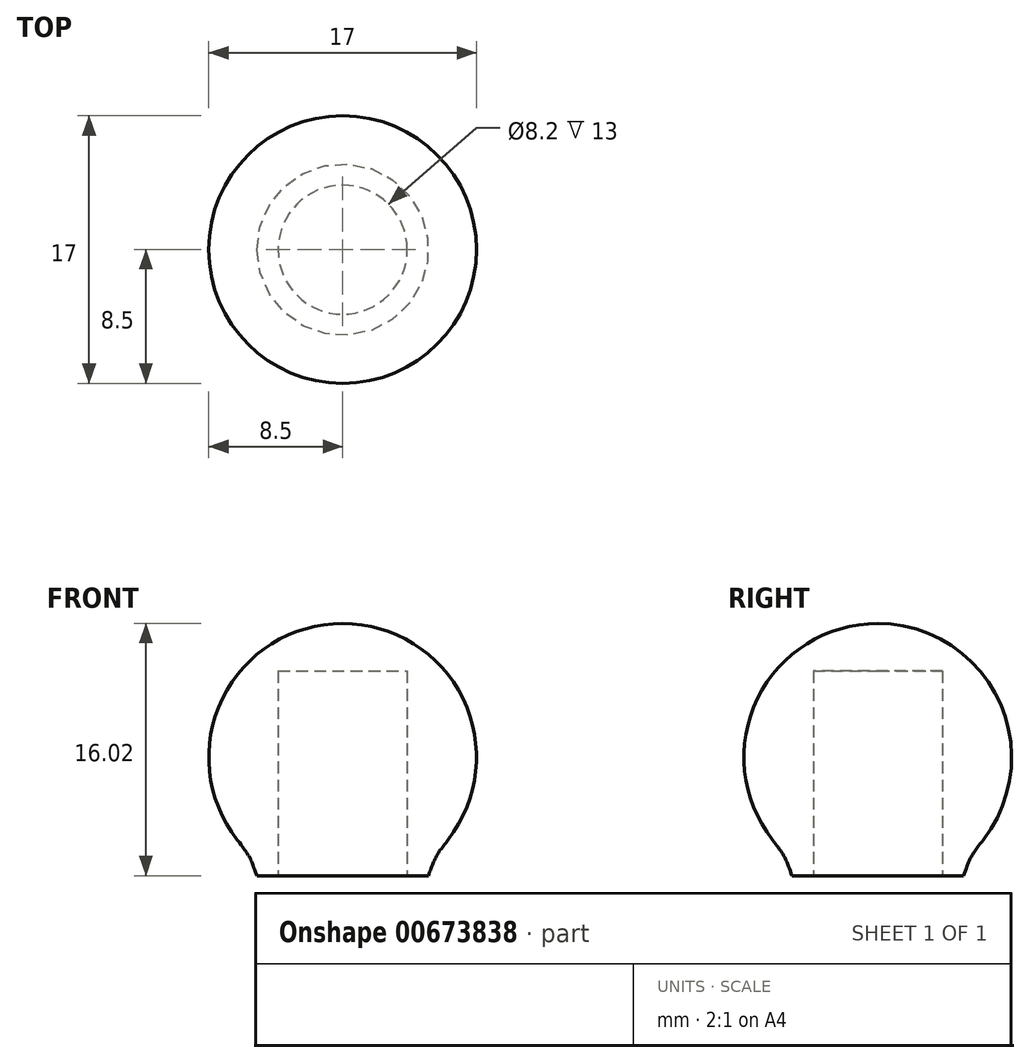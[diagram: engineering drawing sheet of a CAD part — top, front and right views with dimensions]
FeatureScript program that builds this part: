
annotation { "Feature Type Name" : "Feature", "Feature Type Description" : "" }
export const myFeature = defineFeature(function(context is Context, id is Id, definition is map)
    precondition{}
    {
        {
            var Q0;
            Q0=qCreatedBy(makeId("Right.planeOp"),FACE);
            var sketch = newSketch(context, id + "F0", { "sketchPlane" : qUnion([Q0])});
            skLineSegment(sketch, "E0", {"start": v(0, 0) * mm, "end": v(4.1, 0) * mm, "construction": true});
            skArc(sketch, "E1", {"start": v(5.45, 0) * mm, "mid": v(8, 9.42) * mm, "end": v(0, 15.02) * mm});
            skLineSegment(sketch, "E2", {"start": v(0, 0) * mm, "end": v(0, 15.02) * mm, "construction": true});
            skLineSegment(sketch, "E3", {"start": v(4.1, 12) * mm, "end": v(0, 12) * mm});
            skLineSegment(sketch, "E4", {"start": v(0, 12) * mm, "end": v(0, 15.02) * mm});
            skLineSegment(sketch, "E5", {"start": v(4.1, 12) * mm, "end": v(4.1, -1) * mm});
            skLineSegment(sketch, "E6", {"start": v(4.1, -1) * mm, "end": v(5.45, -1) * mm});
            skLineSegment(sketch, "E7", {"start": v(5.45, -1) * mm, "end": v(5.45, 0) * mm});
            skLineSegment(sketch, "E8", {"start": v(5.45, 0) * mm, "end": v(4.1, 0) * mm, "construction": true});
            skSolve(sketch);
        }
        {
            var Q0;
            Q0=makeQuery(id+"F0.imprint","IMPRINT",FACE,{"disambiguationData":[TD([[makeQuery(id+"F0.imprint","IMPRINT",EDGE,{"derivedFrom":sQuery(id+"F0.wireOp",EDGE,"E1")}),1.0]])]});
            var Q1;
            Q1=sQuery(id+"F0.wireOp",EDGE,"E4");
            revolve(context, id + "F1", {"entities" : qUnion([Q0]), "axis" : qUnion([Q1]), "revolveType" : RevolveType.FULL});
        }
        {
            var Q0;
            Q0=makeQuery(id+"F1.opRevolve","SWEPT_EDGE",EDGE,{"disambiguationData":[OSD([sQuery(id+"F0.wireOp",EDGE,"E1"),sQuery(id+"F0.wireOp",EDGE,"E7")])]});
            fillet(context, id + "F2", {"entities" : qUnion([Q0]), "radius" : 8 * mm, "tangentPropagation" : true, "rho" : .7, "crossSection" : FilletCrossSection.CONIC, "allowEdgeOverflow" : false});
        }
    });
